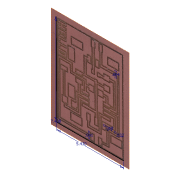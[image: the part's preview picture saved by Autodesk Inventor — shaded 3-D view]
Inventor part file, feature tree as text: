
AUTODESK INVENTOR PART (.ipt)
format: ipt  version: unknown  size: 1,605,120 bytes
history: native  units: in
note: dims shown in document units (in); Inventor stores cm internally (conversion verified against a paired STEP export)
features: sketch x1, other x1
ambient origin geometry x8: Origin, YZ Plane, XZ Plane, XY Plane, X Axis, Y Axis, Z Axis, Center Point
feature tree (2):
  sketch  "Sketch1"  dims[d1=5.43in d2=7.4078in d3=0.0317in d4=0.0681in d5=0.0414in d6=0.0637in]
  other  "Image1"
